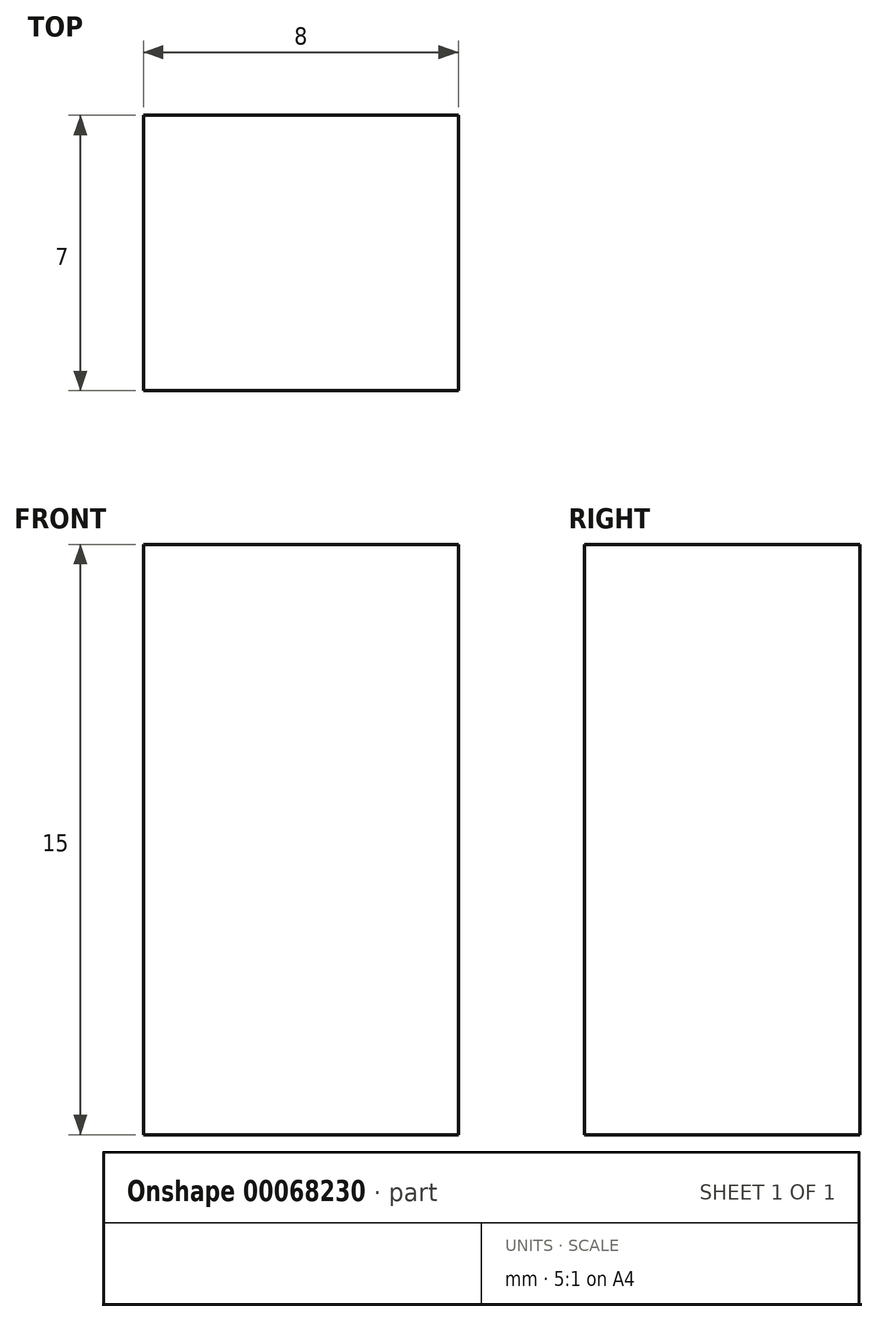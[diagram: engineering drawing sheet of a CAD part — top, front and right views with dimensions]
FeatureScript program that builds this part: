
annotation { "Feature Type Name" : "Feature", "Feature Type Description" : "" }
export const myFeature = defineFeature(function(context is Context, id is Id, definition is map)
    precondition{}
    {
        {
            var Q0;
            Q0=qCreatedBy(makeId("Front.planeOp"),FACE);
            var sketch = newSketch(context, id + "F0", { "sketchPlane" : qUnion([Q0])});
            skLineSegment(sketch, "E0.bottom", {"start": v(-4, 7.5) * mm, "end": v(4, 7.5) * mm});
            skLineSegment(sketch, "E0.top", {"start": v(-4, -7.5) * mm, "end": v(4, -7.5) * mm});
            skLineSegment(sketch, "E0.left", {"start": v(-4, 7.5) * mm, "end": v(-4, -7.5) * mm});
            skLineSegment(sketch, "E0.right", {"start": v(4, 7.5) * mm, "end": v(4, -7.5) * mm});
            skPoint(sketch, "E0.middle", {"position": v(0, 0) * mm});
            skSolve(sketch);
        }
        {
            var Q0;
            Q0=makeQuery(id+"F0.imprint","IMPRINT",FACE,{"disambiguationData":[TD([[makeQuery(id+"F0.imprint","IMPRINT",EDGE,{"derivedFrom":sQuery(id+"F0.wireOp",EDGE,"E0.bottom")}),-1.0]])]});
            extrude(context, id + "F1", {"entities" : qUnion([Q0]), "depth" : 7 * mm});
        }
    });
